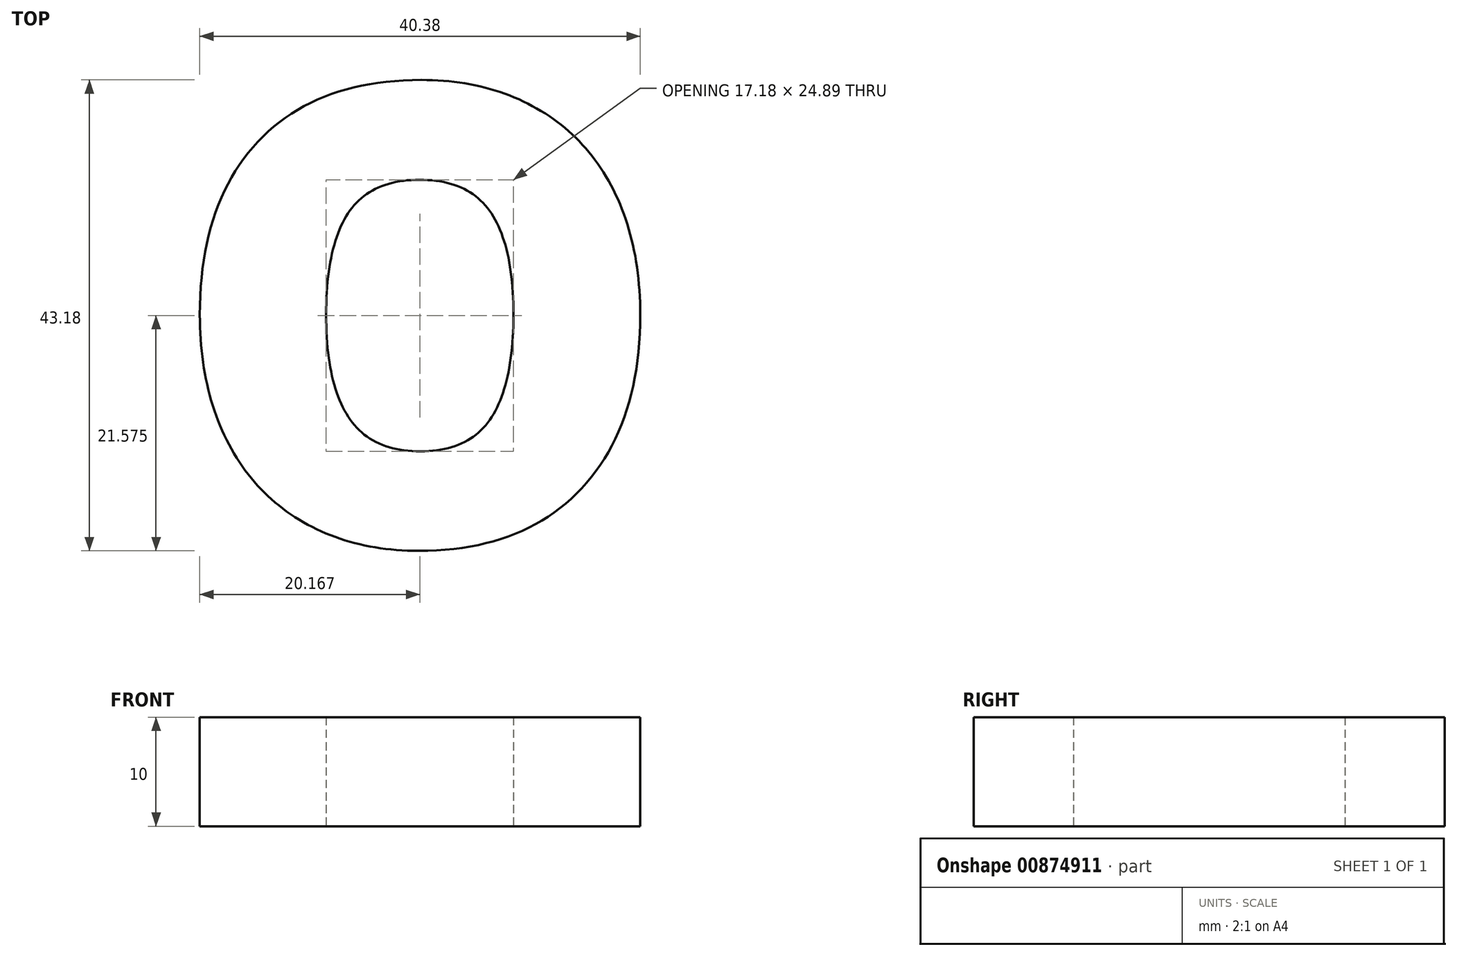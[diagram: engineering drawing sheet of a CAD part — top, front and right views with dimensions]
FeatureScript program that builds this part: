
annotation { "Feature Type Name" : "Feature", "Feature Type Description" : "" }
export const myFeature = defineFeature(function(context is Context, id is Id, definition is map)
    precondition{}
    {
        {
            var Q0;
            Q0=qCreatedBy(makeId("Top.planeOp"),FACE);
            var sketch = newSketch(context, id + "F0", { "sketchPlane" : qUnion([Q0])});
            skText(sketch, "E0", { "text": "o", "fontName": "OpenSans-Bold.ttf"});
            const initialGuessF0  = {"E0": [0, 0, 1, 0, 0.05493]};
            skSetInitialGuess(sketch, initialGuessF0);
            skSolve(sketch);
        }
        {
            var Q0;
            Q0 = qSketchRegion(id + "F0", true);
            extrude(context, id + "F1", {"entities" : qUnion([Q0]), "depth" : 10 * mm, "offsetDistance" : 25 * mm});
        }
    });
